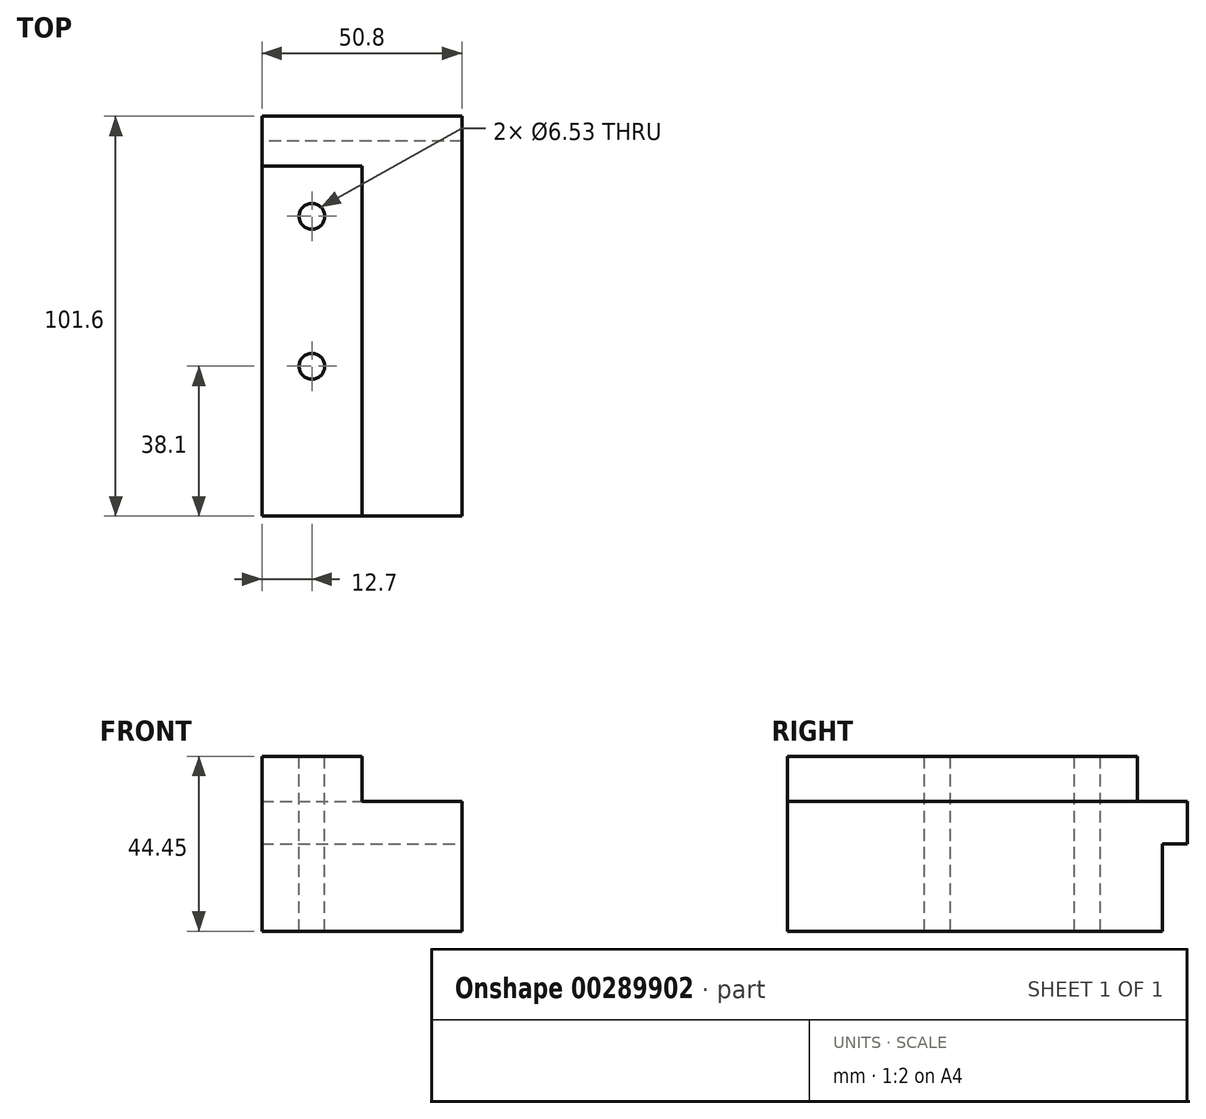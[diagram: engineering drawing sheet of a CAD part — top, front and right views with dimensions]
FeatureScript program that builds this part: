
annotation { "Feature Type Name" : "Feature", "Feature Type Description" : "" }
export const myFeature = defineFeature(function(context is Context, id is Id, definition is map)
    precondition{}
    {
        {
            var Q0;
            Q0=qCreatedBy(makeId("Front.planeOp"),FACE);
            var sketch = newSketch(context, id + "F0", { "sketchPlane" : qUnion([Q0])});
            skLineSegment(sketch, "E0", {"start": v(0, 0) * mm, "end": v(25.4, 0) * mm});
            skLineSegment(sketch, "E1", {"start": v(25.4, 0) * mm, "end": v(25.4, -11.43) * mm});
            skLineSegment(sketch, "E2", {"start": v(25.4, -11.43) * mm, "end": v(50.8, -11.43) * mm});
            skLineSegment(sketch, "E3", {"start": v(50.8, -11.43) * mm, "end": v(50.8, -44.45) * mm});
            skLineSegment(sketch, "E4", {"start": v(50.8, -44.45) * mm, "end": v(0, -44.45) * mm});
            skLineSegment(sketch, "E5", {"start": v(0, -44.45) * mm, "end": v(0, 0) * mm});
            skSolve(sketch);
        }
        {
            var Q0;
            Q0=makeQuery(id+"F0.imprint","IMPRINT",FACE,{"disambiguationData":[TD([[makeQuery(id+"F0.imprint","IMPRINT",EDGE,{"derivedFrom":sQuery(id+"F0.wireOp",EDGE,"E0")}),-1.0]])]});
            extrude(context, id + "F1", {"entities" : qUnion([Q0]), "oppositeDirection" : true, "depth" : 101.6 * mm});
        }
        {
            var Q0;
            Q0=makeQuery(id+"F1.opExtrude","CAP_FACE",FACE,{"disambiguationData":[OSD([sQuery(id+"F0.wireOp",EDGE,"E0"),sQuery(id+"F0.wireOp",EDGE,"E1"),sQuery(id+"F0.wireOp",EDGE,"E2"),sQuery(id+"F0.wireOp",EDGE,"E3"),sQuery(id+"F0.wireOp",EDGE,"E4"),sQuery(id+"F0.wireOp",EDGE,"E5")])],"isStart":false});
            var sketch = newSketch(context, id + "F2", { "sketchPlane" : qUnion([Q0])});
            skLineSegment(sketch, "E6.bottom", {"start": v(0, -44.45) * mm, "end": v(-50.8, -44.45) * mm});
            skLineSegment(sketch, "E6.top", {"start": v(0, -22.22) * mm, "end": v(-50.8, -22.23) * mm});
            skLineSegment(sketch, "E6.left", {"start": v(0, -44.45) * mm, "end": v(0, -22.22) * mm});
            skLineSegment(sketch, "E6.right", {"start": v(-50.8, -44.45) * mm, "end": v(-50.8, -22.23) * mm});
            skSolve(sketch);
        }
        {
            var Q0;
            Q0=makeQuery(id+"F2.imprint","IMPRINT",FACE,{"disambiguationData":[TD([[makeQuery(id+"F2.imprint","IMPRINT",EDGE,{"derivedFrom":sQuery(id+"F2.wireOp",EDGE,"E6.bottom")}),1.0]])]});
            extrude(context, id + "F3", {"entities" : qUnion([Q0]), "operationType" : NewBodyOperationType.REMOVE, "oppositeDirection" : true, "depth" : 6.35 * mm});
        }
        {
            var Q0;
            Q0=makeQuery(id+"F1.opExtrude","SWEPT_FACE",FACE,{"disambiguationData":[OSD([sQuery(id+"F0.wireOp",EDGE,"E0")])]});
            var sketch = newSketch(context, id + "F4", { "sketchPlane" : qUnion([Q0])});
            skLineSegment(sketch, "E7.bottom", {"start": v(0, 101.6) * mm, "end": v(25.4, 101.6) * mm});
            skLineSegment(sketch, "E7.top", {"start": v(0, 88.9) * mm, "end": v(25.4, 88.9) * mm});
            skLineSegment(sketch, "E7.left", {"start": v(0, 101.6) * mm, "end": v(0, 88.9) * mm});
            skLineSegment(sketch, "E7.right", {"start": v(25.4, 101.6) * mm, "end": v(25.4, 88.9) * mm});
            skSolve(sketch);
        }
        {
            var Q0;
            Q0=makeQuery(id+"F4.imprint","IMPRINT",FACE,{"disambiguationData":[TD([[makeQuery(id+"F4.imprint","IMPRINT",EDGE,{"derivedFrom":sQuery(id+"F4.wireOp",EDGE,"E7.bottom")}),-1.0]])]});
            var Q1;
            Q1=makeQuery(id+"F1.opExtrude","SWEPT_FACE",FACE,{"disambiguationData":[OSD([sQuery(id+"F0.wireOp",EDGE,"E2")])]});
            extrude(context, id + "F5", {"entities" : qUnion([Q0]), "operationType" : NewBodyOperationType.REMOVE, "endBound" : BoundingType.UP_TO_SURFACE, "oppositeDirection" : true, "endBoundEntityFace" : qUnion([Q1]), "depth" : 25.4 * mm});
        }
        {
            var Q0;
            Q0=makeQuery(id+"F1.opExtrude","SWEPT_FACE",FACE,{"disambiguationData":[OSD([sQuery(id+"F0.wireOp",EDGE,"E0")])]});
            var sketch = newSketch(context, id + "F6", { "sketchPlane" : qUnion([Q0])});
            skLineSegment(sketch, "E8.0", {"start": v(0, 101.6) * mm, "end": v(50.8, 101.6) * mm, "construction": true});
            skPoint(sketch, "E9", {"position": v(12.7, 76.2) * mm});
            skPoint(sketch, "E10", {"position": v(12.7, 38.1) * mm});
            skSolve(sketch);
        }
        {
            var Q0;
            Q0=sQuery(id+"F6.wireOp",VERTEX,"E9");
            var Q1;
            Q1=sQuery(id+"F6.wireOp",VERTEX,"E10");
            var Q2;
            Q2=makeQuery(id+"F1.opExtrude","SWEPT_BODY",BODY,{"disambiguationData":[OSD([sQuery(id+"F0.wireOp",EDGE,"E0"),sQuery(id+"F0.wireOp",EDGE,"E1"),sQuery(id+"F0.wireOp",EDGE,"E2"),sQuery(id+"F0.wireOp",EDGE,"E3"),sQuery(id+"F0.wireOp",EDGE,"E4"),sQuery(id+"F0.wireOp",EDGE,"E5")])]});
            hole(context, id + "F7", {"style" : HoleStyle.SIMPLE, "endStyle" : HoleEndStyle.THROUGH, "holeDiameter" : 6.53 * mm, "tappedDepth" : 12.7 * mm, "tapClearance" : 3, "startFromSketch" : true, "locations" : qUnion([Q0, Q1]), "scope" : qUnion([Q2])});
        }
    });
